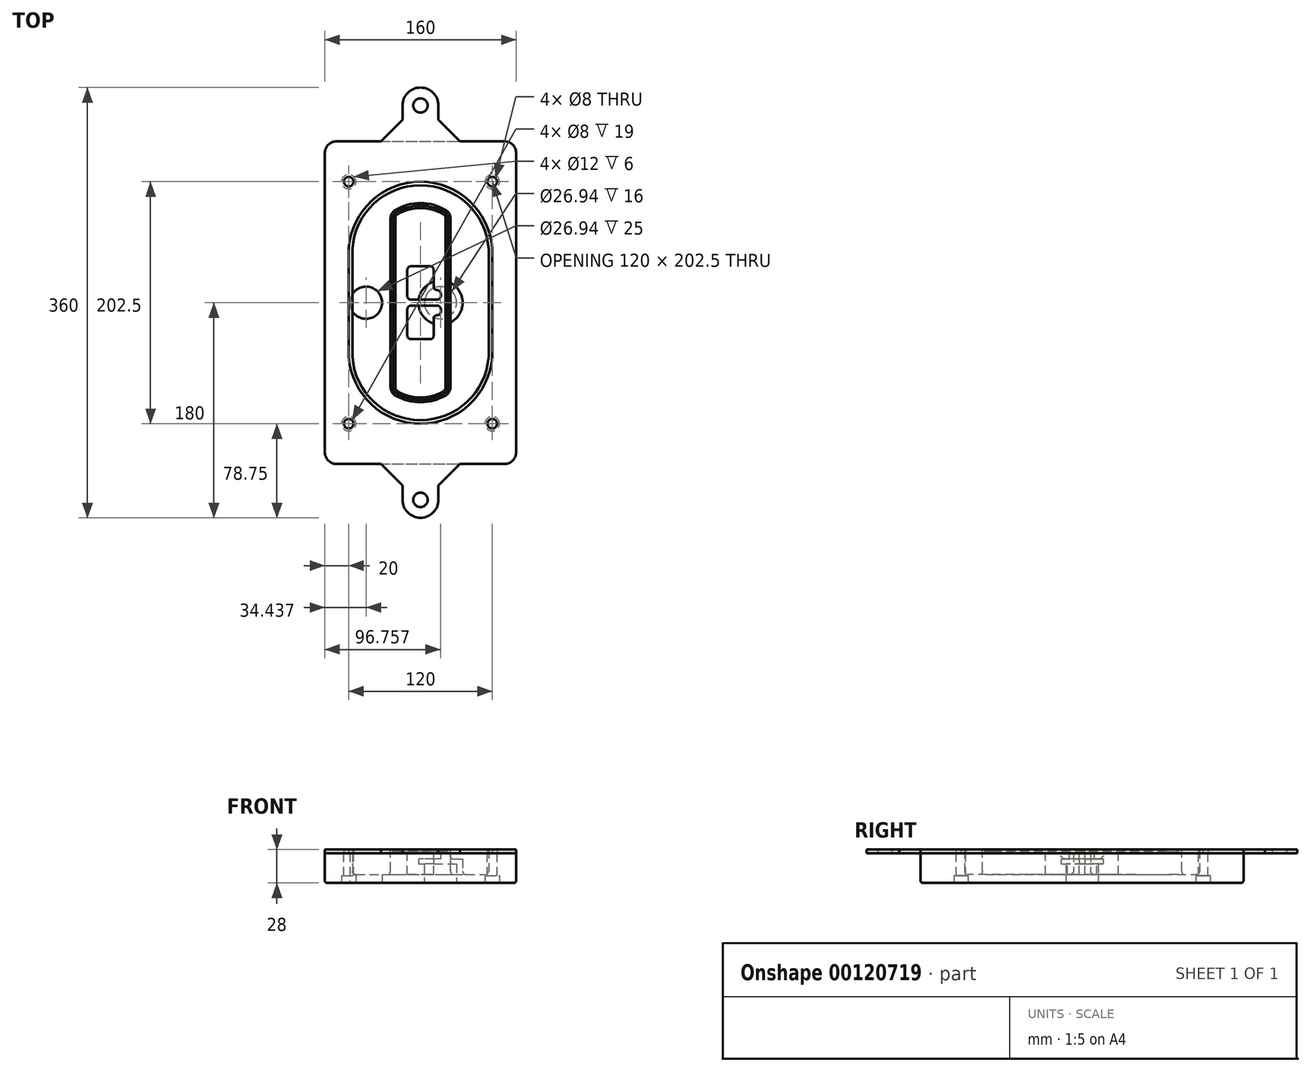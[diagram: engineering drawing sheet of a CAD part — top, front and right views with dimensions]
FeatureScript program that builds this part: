
annotation { "Feature Type Name" : "Feature", "Feature Type Description" : "" }
export const myFeature = defineFeature(function(context is Context, id is Id, definition is map)
    precondition{}
    {
        {
            var Q0;
            Q0=qCreatedBy(makeId("Top.planeOp"),FACE);
            var sketch = newSketch(context, id + "F0", { "sketchPlane" : qUnion([Q0])});
            skPoint(sketch, "E0.rect.middle", {"position": v(0, 0) * mm});
            skLineSegment(sketch, "E1.bottom", {"start": v(-70, -135) * mm, "end": v(70, -135) * mm});
            skLineSegment(sketch, "E1.top", {"start": v(-70, 135) * mm, "end": v(70, 135) * mm});
            skLineSegment(sketch, "E1.left", {"start": v(-80, -125) * mm, "end": v(-80, 125) * mm});
            skLineSegment(sketch, "E1.right", {"start": v(80, -125) * mm, "end": v(80, 125) * mm});
            skLineSegment(sketch, "E2", {"start": v(-80, 135) * mm, "end": v(80, -135) * mm, "construction": true});
            skLineSegment(sketch, "E3", {"start": v(80, 135) * mm, "end": v(-80, -135) * mm, "construction": true});
            skCircle(sketch, "E4", {"center": v(-60, 101.25) * mm, "radius": 4 * mm});
            skCircle(sketch, "E5", {"center": v(60, 101.25) * mm, "radius": 4 * mm});
            skCircle(sketch, "E6", {"center": v(60, -101.25) * mm, "radius": 4 * mm});
            skCircle(sketch, "E7", {"center": v(-60, -101.25) * mm, "radius": 4 * mm});
            skLineSegment(sketch, "E8", {"start": v(-60, 101.25) * mm, "end": v(60, 101.25) * mm, "construction": true});
            skLineSegment(sketch, "E9", {"start": v(60, 101.25) * mm, "end": v(60, -101.25) * mm, "construction": true});
            skLineSegment(sketch, "E10", {"start": v(60, -101.25) * mm, "end": v(-60, -101.25) * mm, "construction": true});
            skLineSegment(sketch, "E11", {"start": v(-60, -101.25) * mm, "end": v(-60, 101.25) * mm, "construction": true});
            skLineSegment(sketch, "E12", {"start": v(-60, 44.66) * mm, "end": v(-60, -44.66) * mm});
            skLineSegment(sketch, "E13", {"start": v(60, 44.66) * mm, "end": v(60, -44.66) * mm});
            skArc(sketch, "E14", {"start": v(59.98, 45.37) * mm, "mid": v(0, 101.25) * mm, "end": v(-59.98, 45.37) * mm});
            skArc(sketch, "E15", {"start": v(-59.98, -45.37) * mm, "mid": v(0, -101.25) * mm, "end": v(59.98, -45.37) * mm});
            skLineSegment(sketch, "E16", {"start": v(-60, 0) * mm, "end": v(60, 0) * mm, "construction": true});
            skPoint(sketch, "E17.visualSharp", {"position": v(-60, -45) * mm});
            skArc(sketch, "E17.filletArc", {"start": v(-60, -44.66) * mm, "mid": v(-60, -45.02) * mm, "end": v(-59.98, -45.37) * mm});
            skPoint(sketch, "E18.visualSharp", {"position": v(-60, 45) * mm});
            skArc(sketch, "E18.filletArc", {"start": v(-59.98, 45.37) * mm, "mid": v(-60, 45.02) * mm, "end": v(-60, 44.66) * mm});
            skPoint(sketch, "E19.visualSharp", {"position": v(60, 45) * mm});
            skArc(sketch, "E19.filletArc", {"start": v(60, 44.66) * mm, "mid": v(60, 45.02) * mm, "end": v(59.98, 45.37) * mm});
            skPoint(sketch, "E20.visualSharp", {"position": v(60, -45) * mm});
            skArc(sketch, "E20.filletArc", {"start": v(59.98, -45.37) * mm, "mid": v(60, -45.02) * mm, "end": v(60, -44.66) * mm});
            skPoint(sketch, "E21.visualSharp", {"position": v(-80, 135) * mm});
            skArc(sketch, "E21.filletArc", {"start": v(-70, 135) * mm, "mid": v(-77.07, 132.07) * mm, "end": v(-80, 125) * mm});
            skPoint(sketch, "E22.visualSharp", {"position": v(80, 135) * mm});
            skArc(sketch, "E22.filletArc", {"start": v(80, 125) * mm, "mid": v(77.07, 132.07) * mm, "end": v(70, 135) * mm});
            skPoint(sketch, "E23.visualSharp", {"position": v(80, -135) * mm});
            skArc(sketch, "E23.filletArc", {"start": v(70, -135) * mm, "mid": v(77.07, -132.07) * mm, "end": v(80, -125) * mm});
            skPoint(sketch, "E24.visualSharp", {"position": v(-80, -135) * mm});
            skArc(sketch, "E24.filletArc", {"start": v(-80, -125) * mm, "mid": v(-77.07, -132.07) * mm, "end": v(-70, -135) * mm});
            skArc(sketch, "E25.0", {"start": v(57, 44.66) * mm, "mid": v(57, 44.9) * mm, "end": v(56.98, 45.16) * mm});
            skLineSegment(sketch, "E25.1", {"start": v(57, 44.66) * mm, "end": v(57, -44.66) * mm});
            skArc(sketch, "E25.2", {"start": v(56.98, -45.16) * mm, "mid": v(57, -44.9) * mm, "end": v(57, -44.66) * mm});
            skArc(sketch, "E25.3", {"start": v(-56.98, -45.16) * mm, "mid": v(0, -98.25) * mm, "end": v(56.98, -45.16) * mm});
            skArc(sketch, "E25.4", {"start": v(-57, -44.66) * mm, "mid": v(-57, -44.9) * mm, "end": v(-56.98, -45.16) * mm});
            skArc(sketch, "E25.5", {"start": v(56.98, 45.16) * mm, "mid": v(0, 98.25) * mm, "end": v(-56.98, 45.16) * mm});
            skLineSegment(sketch, "E25.6", {"start": v(-57, 44.66) * mm, "end": v(-57, -44.66) * mm});
            skArc(sketch, "E25.7", {"start": v(-56.98, 45.16) * mm, "mid": v(-57, 44.9) * mm, "end": v(-57, 44.66) * mm});
            skArc(sketch, "E26.0", {"start": v(-63.97, 45.65) * mm, "mid": v(-64, 45.16) * mm, "end": v(-64, 44.66) * mm});
            skArc(sketch, "E26.1", {"start": v(63.97, 45.65) * mm, "mid": v(0, 105.25) * mm, "end": v(-63.97, 45.65) * mm});
            skArc(sketch, "E26.2", {"start": v(64, 44.66) * mm, "mid": v(64, 45.16) * mm, "end": v(63.97, 45.65) * mm});
            skLineSegment(sketch, "E26.3", {"start": v(64, 44.66) * mm, "end": v(64, -44.66) * mm});
            skArc(sketch, "E26.4", {"start": v(63.97, -45.65) * mm, "mid": v(64, -45.16) * mm, "end": v(64, -44.66) * mm});
            skLineSegment(sketch, "E26.5", {"start": v(-64, 44.66) * mm, "end": v(-64, -44.66) * mm});
            skArc(sketch, "E26.6", {"start": v(-63.97, -45.65) * mm, "mid": v(0, -105.25) * mm, "end": v(63.97, -45.65) * mm});
            skArc(sketch, "E26.7", {"start": v(-64, -44.66) * mm, "mid": v(-64, -45.16) * mm, "end": v(-63.97, -45.65) * mm});
            skSolve(sketch);
        }
        {
            var Q0;
            Q0=makeQuery(id+"F0.imprint","IMPRINT",FACE,{"disambiguationData":[TD([[makeQuery(id+"F0.imprint","IMPRINT",EDGE,{"derivedFrom":sQuery(id+"F0.wireOp",EDGE,"E1.bottom")}),1.0]])]});
            var Q1;
            Q1=makeQuery(id+"F0.imprint","IMPRINT",FACE,{"disambiguationData":[TD([[makeQuery(id+"F0.imprint","IMPRINT",EDGE,{"derivedFrom":sQuery(id+"F0.wireOp",EDGE,"E12")}),1.0]])]});
            var Q2;
            Q2=makeQuery(id+"F0.imprint","IMPRINT",FACE,{"disambiguationData":[TD([[makeQuery(id+"F0.imprint","IMPRINT",EDGE,{"derivedFrom":sQuery(id+"F0.wireOp",EDGE,"E25.0")}),1.0]])]});
            var Q3;
            Q3=makeQuery(id+"F0.imprint","IMPRINT",FACE,{"disambiguationData":[TD([[makeQuery(id+"F0.imprint","IMPRINT",EDGE,{"derivedFrom":sQuery(id+"F0.wireOp",EDGE,"E12")}),-1.0]])]});
            extrude(context, id + "F1", {"entities" : qUnion([Q0, Q1, Q2, Q3]), "oppositeDirection" : true, "depth" : 25 * mm});
        }
        {
            var Q0;
            Q0=makeQuery(id+"F0.imprint","IMPRINT",FACE,{"disambiguationData":[TD([[makeQuery(id+"F0.imprint","IMPRINT",EDGE,{"derivedFrom":sQuery(id+"F0.wireOp",EDGE,"E12")}),1.0]])]});
            extrude(context, id + "F2", {"entities" : qUnion([Q0]), "operationType" : NewBodyOperationType.ADD, "depth" : 3 * mm});
        }
        {
            var Q0;
            Q0=makeQuery(id+"F0.imprint","IMPRINT",FACE,{"disambiguationData":[TD([[makeQuery(id+"F0.imprint","IMPRINT",EDGE,{"derivedFrom":sQuery(id+"F0.wireOp",EDGE,"E25.0")}),1.0]])]});
            extrude(context, id + "F3", {"entities" : qUnion([Q0]), "operationType" : NewBodyOperationType.REMOVE, "oppositeDirection" : true, "depth" : 18 * mm});
        }
        {
            var Q0;
            Q0=makeQuery(id+"F2.opExtrude","CAP_FACE",FACE,{"disambiguationData":[OSD([sQuery(id+"F0.wireOp",EDGE,"E12"),sQuery(id+"F0.wireOp",EDGE,"E13"),sQuery(id+"F0.wireOp",EDGE,"E14"),sQuery(id+"F0.wireOp",EDGE,"E15"),sQuery(id+"F0.wireOp",EDGE,"E17.filletArc"),sQuery(id+"F0.wireOp",EDGE,"E18.filletArc"),sQuery(id+"F0.wireOp",EDGE,"E19.filletArc"),sQuery(id+"F0.wireOp",EDGE,"E20.filletArc"),sQuery(id+"F0.wireOp",EDGE,"E25.0"),sQuery(id+"F0.wireOp",EDGE,"E25.1"),sQuery(id+"F0.wireOp",EDGE,"E25.2"),sQuery(id+"F0.wireOp",EDGE,"E25.3"),sQuery(id+"F0.wireOp",EDGE,"E25.4"),sQuery(id+"F0.wireOp",EDGE,"E25.5"),sQuery(id+"F0.wireOp",EDGE,"E25.6"),sQuery(id+"F0.wireOp",EDGE,"E25.7")])],"isStart":false});
            var sketch = newSketch(context, id + "F4", { "sketchPlane" : qUnion([Q0])});
            skArc(sketch, "E27.0", {"start": v(-20.99, -77.65) * mm, "mid": v(0, -83.25) * mm, "end": v(20.99, -77.65) * mm});
            skArc(sketch, "E28.0", {"start": v(20.99, 77.65) * mm, "mid": v(0, 83.25) * mm, "end": v(-20.99, 77.65) * mm});
            skLineSegment(sketch, "E29", {"start": v(-25, 70.71) * mm, "end": v(-25, -70.71) * mm});
            skLineSegment(sketch, "E30", {"start": v(25, 70.71) * mm, "end": v(25, -70.71) * mm});
            skLineSegment(sketch, "E31", {"start": v(-25, 75.03) * mm, "end": v(25, 75.03) * mm, "construction": true});
            skLineSegment(sketch, "E32", {"start": v(-25, -75.03) * mm, "end": v(25, -75.03) * mm, "construction": true});
            skPoint(sketch, "E33.visualSharp", {"position": v(-25, 75.03) * mm});
            skArc(sketch, "E33.filletArc", {"start": v(-20.99, 77.65) * mm, "mid": v(-23.92, 74.72) * mm, "end": v(-25, 70.71) * mm});
            skPoint(sketch, "E34.visualSharp", {"position": v(25, 75.03) * mm});
            skArc(sketch, "E34.filletArc", {"start": v(25, 70.71) * mm, "mid": v(23.92, 74.72) * mm, "end": v(20.99, 77.65) * mm});
            skPoint(sketch, "E35.visualSharp", {"position": v(25, -75.03) * mm});
            skArc(sketch, "E35.filletArc", {"start": v(20.99, -77.65) * mm, "mid": v(23.92, -74.72) * mm, "end": v(25, -70.71) * mm});
            skPoint(sketch, "E36.visualSharp", {"position": v(-25, -75.03) * mm});
            skArc(sketch, "E36.filletArc", {"start": v(-25, -70.71) * mm, "mid": v(-23.92, -74.72) * mm, "end": v(-20.99, -77.65) * mm});
            skArc(sketch, "E37.0", {"start": v(56.98, 45.16) * mm, "mid": v(0, 98.25) * mm, "end": v(-56.98, 45.16) * mm});
            skArc(sketch, "E37.1", {"start": v(-56.98, 45.16) * mm, "mid": v(-57, 44.9) * mm, "end": v(-57, 44.66) * mm});
            skLineSegment(sketch, "E37.2", {"start": v(-57, 44.66) * mm, "end": v(-57, -44.66) * mm});
            skArc(sketch, "E37.3", {"start": v(-57, -44.66) * mm, "mid": v(-57, -44.9) * mm, "end": v(-56.98, -45.16) * mm});
            skArc(sketch, "E37.4", {"start": v(-56.98, -45.16) * mm, "mid": v(0, -98.25) * mm, "end": v(56.98, -45.16) * mm});
            skArc(sketch, "E37.5", {"start": v(56.98, -45.16) * mm, "mid": v(57, -44.9) * mm, "end": v(57, -44.66) * mm});
            skLineSegment(sketch, "E37.6", {"start": v(57, 44.66) * mm, "end": v(57, -44.66) * mm});
            skArc(sketch, "E37.7", {"start": v(57, 44.66) * mm, "mid": v(57, 44.9) * mm, "end": v(56.98, 45.16) * mm});
            skLineSegment(sketch, "E38.0", {"start": v(23, 70.71) * mm, "end": v(23, -70.71) * mm});
            skArc(sketch, "E38.1", {"start": v(19.99, -75.92) * mm, "mid": v(22.2, -73.72) * mm, "end": v(23, -70.71) * mm});
            skArc(sketch, "E38.2", {"start": v(-19.99, -75.92) * mm, "mid": v(0, -81.25) * mm, "end": v(19.99, -75.92) * mm});
            skArc(sketch, "E38.3", {"start": v(-23, -70.71) * mm, "mid": v(-22.2, -73.72) * mm, "end": v(-19.99, -75.92) * mm});
            skLineSegment(sketch, "E38.4", {"start": v(-23, 70.71) * mm, "end": v(-23, -70.71) * mm});
            skArc(sketch, "E38.5", {"start": v(23, 70.71) * mm, "mid": v(22.2, 73.72) * mm, "end": v(19.99, 75.92) * mm});
            skArc(sketch, "E38.6", {"start": v(-19.99, 75.92) * mm, "mid": v(-22.2, 73.72) * mm, "end": v(-23, 70.71) * mm});
            skArc(sketch, "E38.7", {"start": v(19.99, 75.92) * mm, "mid": v(0, 81.25) * mm, "end": v(-19.99, 75.92) * mm});
            skArc(sketch, "E39.0", {"start": v(21, 70.71) * mm, "mid": v(20.46, 72.72) * mm, "end": v(19, 74.18) * mm});
            skLineSegment(sketch, "E39.1", {"start": v(21, 70.71) * mm, "end": v(21, -70.71) * mm});
            skArc(sketch, "E39.2", {"start": v(19, -74.18) * mm, "mid": v(20.46, -72.72) * mm, "end": v(21, -70.71) * mm});
            skArc(sketch, "E39.3", {"start": v(-19, -74.18) * mm, "mid": v(0, -79.25) * mm, "end": v(19, -74.18) * mm});
            skArc(sketch, "E39.4", {"start": v(-21, -70.71) * mm, "mid": v(-20.46, -72.72) * mm, "end": v(-19, -74.18) * mm});
            skArc(sketch, "E39.5", {"start": v(19, 74.18) * mm, "mid": v(0, 79.25) * mm, "end": v(-19, 74.18) * mm});
            skLineSegment(sketch, "E39.6", {"start": v(-21, 70.71) * mm, "end": v(-21, -70.71) * mm});
            skArc(sketch, "E39.7", {"start": v(-19, 74.18) * mm, "mid": v(-20.46, 72.72) * mm, "end": v(-21, 70.71) * mm});
            skLineSegment(sketch, "E40", {"start": v(-25, 0) * mm, "end": v(25, 0) * mm, "construction": true});
            skLineSegment(sketch, "E41", {"start": v(-11, 5.5) * mm, "end": v(-11, 27.5) * mm});
            skLineSegment(sketch, "E42", {"start": v(-8, 30.5) * mm, "end": v(8, 30.5) * mm});
            skLineSegment(sketch, "E43", {"start": v(11, 27.5) * mm, "end": v(11, 13.5) * mm});
            skLineSegment(sketch, "E44", {"start": v(14, 10.5) * mm, "end": v(14, 10.5) * mm});
            skLineSegment(sketch, "E45", {"start": v(17, 7.5) * mm, "end": v(17, 5.5) * mm});
            skLineSegment(sketch, "E46", {"start": v(14, 2.5) * mm, "end": v(-8, 2.5) * mm});
            skPoint(sketch, "E47.visualSharp", {"position": v(-11, 30.5) * mm});
            skArc(sketch, "E47.filletArc", {"start": v(-8, 30.5) * mm, "mid": v(-10.12, 29.62) * mm, "end": v(-11, 27.5) * mm});
            skPoint(sketch, "E48.visualSharp", {"position": v(11, 30.5) * mm});
            skArc(sketch, "E48.filletArc", {"start": v(11, 27.5) * mm, "mid": v(10.12, 29.62) * mm, "end": v(8, 30.5) * mm});
            skPoint(sketch, "E49.visualSharp", {"position": v(11, 10.5) * mm});
            skArc(sketch, "E49.filletArc", {"start": v(11, 13.5) * mm, "mid": v(11.88, 11.38) * mm, "end": v(14, 10.5) * mm});
            skPoint(sketch, "E50.visualSharp", {"position": v(17, 10.5) * mm});
            skArc(sketch, "E50.filletArc", {"start": v(17, 7.5) * mm, "mid": v(16.12, 9.62) * mm, "end": v(14, 10.5) * mm});
            skPoint(sketch, "E51.visualSharp", {"position": v(17, 2.5) * mm});
            skArc(sketch, "E51.filletArc", {"start": v(14, 2.5) * mm, "mid": v(16.12, 3.38) * mm, "end": v(17, 5.5) * mm});
            skPoint(sketch, "E52.visualSharp", {"position": v(-11, 2.5) * mm});
            skArc(sketch, "E52.filletArc", {"start": v(-11, 5.5) * mm, "mid": v(-10.12, 3.38) * mm, "end": v(-8, 2.5) * mm});
            skLineSegment(sketch, "E53.0.MirrorCS", {"start": v(14, -2.5) * mm, "end": v(-8, -2.5) * mm});
            skArc(sketch, "E54.0.MirrorCS", {"start": v(-11, -5.5) * mm, "mid": v(-10.12, -3.38) * mm, "end": v(-8, -2.5) * mm});
            skLineSegment(sketch, "E55.0.MirrorCS", {"start": v(-11, -5.5) * mm, "end": v(-11, -27.5) * mm});
            skArc(sketch, "E56.0.MirrorCS", {"start": v(-8, -30.5) * mm, "mid": v(-10.12, -29.62) * mm, "end": v(-11, -27.5) * mm});
            skLineSegment(sketch, "E57.0.MirrorCS", {"start": v(-8, -30.5) * mm, "end": v(8, -30.5) * mm});
            skArc(sketch, "E58.0.MirrorCS", {"start": v(11, -27.5) * mm, "mid": v(10.12, -29.62) * mm, "end": v(8, -30.5) * mm});
            skLineSegment(sketch, "E59.0.MirrorCS", {"start": v(11, -27.5) * mm, "end": v(11, -13.5) * mm});
            skArc(sketch, "E60.0.MirrorCS", {"start": v(11, -13.5) * mm, "mid": v(11.88, -11.38) * mm, "end": v(14, -10.5) * mm});
            skArc(sketch, "E61.0.MirrorCS", {"start": v(17, -7.5) * mm, "mid": v(16.12, -9.62) * mm, "end": v(14, -10.5) * mm});
            skLineSegment(sketch, "E62.0.MirrorCS", {"start": v(17, -7.5) * mm, "end": v(17, -5.5) * mm});
            skArc(sketch, "E63.0.MirrorCS", {"start": v(14, -2.5) * mm, "mid": v(16.12, -3.38) * mm, "end": v(17, -5.5) * mm});
            skSolve(sketch);
        }
        {
            var Q0;
            Q0=makeQuery(id+"F4.imprint","IMPRINT",FACE,{"disambiguationData":[TD([[makeQuery(id+"F4.imprint","IMPRINT",EDGE,{"derivedFrom":sQuery(id+"F4.wireOp",EDGE,"E27.0")}),1.0]])]});
            var Q1;
            Q1=makeQuery(id+"F4.imprint","IMPRINT",FACE,{"disambiguationData":[TD([[makeQuery(id+"F4.imprint","IMPRINT",EDGE,{"derivedFrom":sQuery(id+"F4.wireOp",EDGE,"E38.0")}),-1.0]])]});
            var Q2;
            Q2=makeQuery(id+"F4.imprint","IMPRINT",FACE,{"disambiguationData":[TD([[makeQuery(id+"F4.imprint","IMPRINT",EDGE,{"derivedFrom":sQuery(id+"F4.wireOp",EDGE,"E39.0")}),1.0]])]});
            extrude(context, id + "F5", {"entities" : qUnion([Q0, Q1, Q2]), "operationType" : NewBodyOperationType.ADD, "endBound" : BoundingType.UP_TO_NEXT, "oppositeDirection" : true, "depth" : 25 * mm});
        }
        {
            var Q0;
            Q0=makeQuery(id+"F4.imprint","IMPRINT",FACE,{"disambiguationData":[TD([[makeQuery(id+"F4.imprint","IMPRINT",EDGE,{"derivedFrom":sQuery(id+"F4.wireOp",EDGE,"E38.0")}),-1.0]])]});
            extrude(context, id + "F6", {"entities" : qUnion([Q0]), "operationType" : NewBodyOperationType.REMOVE, "oppositeDirection" : true, "depth" : 2 * mm});
        }
        {
            var Q0;
            Q0=makeQuery(id+"F1.opExtrude","CAP_FACE",FACE,{"disambiguationData":[OSD([sQuery(id+"F0.wireOp",EDGE,"E1.bottom"),sQuery(id+"F0.wireOp",EDGE,"E1.top"),sQuery(id+"F0.wireOp",EDGE,"E1.left"),sQuery(id+"F0.wireOp",EDGE,"E1.right"),sQuery(id+"F0.wireOp",EDGE,"E4"),sQuery(id+"F0.wireOp",EDGE,"E5"),sQuery(id+"F0.wireOp",EDGE,"E6"),sQuery(id+"F0.wireOp",EDGE,"E7"),sQuery(id+"F0.wireOp",EDGE,"E21.filletArc"),sQuery(id+"F0.wireOp",EDGE,"E22.filletArc"),sQuery(id+"F0.wireOp",EDGE,"E23.filletArc"),sQuery(id+"F0.wireOp",EDGE,"E24.filletArc")])],"isStart":false});
            var sketch = newSketch(context, id + "F7", { "sketchPlane" : qUnion([Q0])});
            skCircle(sketch, "E64", {"center": v(16.76, 0) * mm, "radius": 13.47 * mm});
            skCircle(sketch, "E65", {"center": v(-45.56, 0) * mm, "radius": 13.47 * mm});
            skLineSegment(sketch, "E66", {"start": v(80, 0) * mm, "end": v(-80, 0) * mm});
            skCircle(sketch, "E67", {"center": v(16.76, 0) * mm, "radius": 18.47 * mm});
            skCircle(sketch, "E68", {"center": v(60, -101.25) * mm, "radius": 6 * mm});
            skCircle(sketch, "E69", {"center": v(-60, -101.25) * mm, "radius": 6 * mm});
            skCircle(sketch, "E70", {"center": v(-60, 101.25) * mm, "radius": 6 * mm});
            skCircle(sketch, "E71", {"center": v(60, 101.25) * mm, "radius": 6 * mm});
            skSolve(sketch);
        }
        {
            var Q0;
            {var subQ1=sQuery(id+"F7.wireOp",EDGE,"E66");var subQ4=sQuery(id+"F7.wireOp",EDGE,"E64");var subQ6=makeQuery(id+"F7.imprint","INTERSECT",VERTEX,{"disambiguationData":[OD(0.0)],"derivedFrom":[subQ4,subQ1]});Q0=makeQuery(id+"F7.imprint","IMPRINT",FACE,{"disambiguationData":[TD([[makeQuery(id+"F7.imprint","IMPRINT",EDGE,{"disambiguationData":[TD([[subQ6,-1.0]])],"derivedFrom":subQ4}),-1.0]])]});}
            var Q1;
            {var subQ0=sQuery(id+"F7.wireOp",EDGE,"E66");var subQ1=sQuery(id+"F7.wireOp",EDGE,"E64");var subQ3=makeQuery(id+"F7.imprint","INTERSECT",VERTEX,{"disambiguationData":[OD(0.0)],"derivedFrom":[subQ1,subQ0]});Q1=makeQuery(id+"F7.imprint","IMPRINT",FACE,{"disambiguationData":[TD([[makeQuery(id+"F7.imprint","IMPRINT",EDGE,{"disambiguationData":[TD([[subQ3,-1.0]])],"derivedFrom":subQ1}),1.0]])]});}
            var Q2;
            {var subQ0=sQuery(id+"F7.wireOp",EDGE,"E66");var subQ1=sQuery(id+"F7.wireOp",EDGE,"E64");var subQ3=makeQuery(id+"F7.imprint","INTERSECT",VERTEX,{"disambiguationData":[OD(0.0)],"derivedFrom":[subQ1,subQ0]});Q2=makeQuery(id+"F7.imprint","IMPRINT",FACE,{"disambiguationData":[TD([[makeQuery(id+"F7.imprint","IMPRINT",EDGE,{"disambiguationData":[TD([[subQ3,1.0]])],"derivedFrom":subQ1}),1.0]])]});}
            var Q3;
            {var subQ1=sQuery(id+"F7.wireOp",EDGE,"E66");var subQ4=sQuery(id+"F7.wireOp",EDGE,"E64");var subQ6=makeQuery(id+"F7.imprint","INTERSECT",VERTEX,{"disambiguationData":[OD(0.0)],"derivedFrom":[subQ4,subQ1]});Q3=makeQuery(id+"F7.imprint","IMPRINT",FACE,{"disambiguationData":[TD([[makeQuery(id+"F7.imprint","IMPRINT",EDGE,{"disambiguationData":[TD([[subQ6,1.0]])],"derivedFrom":subQ4}),-1.0]])]});}
            extrude(context, id + "F8", {"entities" : qUnion([Q0, Q1, Q2, Q3]), "operationType" : NewBodyOperationType.ADD, "oppositeDirection" : true, "depth" : 20 * mm});
        }
        {
            var Q0;
            {var subQ0=sQuery(id+"F7.wireOp",EDGE,"E66");var subQ1=sQuery(id+"F7.wireOp",EDGE,"E64");var subQ3=makeQuery(id+"F7.imprint","INTERSECT",VERTEX,{"disambiguationData":[OD(0.0)],"derivedFrom":[subQ1,subQ0]});Q0=makeQuery(id+"F7.imprint","IMPRINT",FACE,{"disambiguationData":[TD([[makeQuery(id+"F7.imprint","IMPRINT",EDGE,{"disambiguationData":[TD([[subQ3,-1.0]])],"derivedFrom":subQ1}),1.0]])]});}
            var Q1;
            {var subQ0=sQuery(id+"F7.wireOp",EDGE,"E66");var subQ1=sQuery(id+"F7.wireOp",EDGE,"E64");var subQ3=makeQuery(id+"F7.imprint","INTERSECT",VERTEX,{"disambiguationData":[OD(0.0)],"derivedFrom":[subQ1,subQ0]});Q1=makeQuery(id+"F7.imprint","IMPRINT",FACE,{"disambiguationData":[TD([[makeQuery(id+"F7.imprint","IMPRINT",EDGE,{"disambiguationData":[TD([[subQ3,1.0]])],"derivedFrom":subQ1}),1.0]])]});}
            extrude(context, id + "F9", {"entities" : qUnion([Q0, Q1]), "operationType" : NewBodyOperationType.REMOVE, "oppositeDirection" : true, "depth" : 16 * mm});
        }
        {
            var Q0;
            {var subQ0=sQuery(id+"F7.wireOp",EDGE,"E66");var subQ1=sQuery(id+"F7.wireOp",EDGE,"E65");var subQ3=makeQuery(id+"F7.imprint","INTERSECT",VERTEX,{"disambiguationData":[OD(0.0)],"derivedFrom":[subQ1,subQ0]});Q0=makeQuery(id+"F7.imprint","IMPRINT",FACE,{"disambiguationData":[TD([[makeQuery(id+"F7.imprint","IMPRINT",EDGE,{"disambiguationData":[TD([[subQ3,-1.0]])],"derivedFrom":subQ1}),1.0]])]});}
            var Q1;
            {var subQ0=sQuery(id+"F7.wireOp",EDGE,"E66");var subQ1=sQuery(id+"F7.wireOp",EDGE,"E65");var subQ3=makeQuery(id+"F7.imprint","INTERSECT",VERTEX,{"disambiguationData":[OD(0.0)],"derivedFrom":[subQ1,subQ0]});Q1=makeQuery(id+"F7.imprint","IMPRINT",FACE,{"disambiguationData":[TD([[makeQuery(id+"F7.imprint","IMPRINT",EDGE,{"disambiguationData":[TD([[subQ3,1.0]])],"derivedFrom":subQ1}),1.0]])]});}
            extrude(context, id + "F10", {"entities" : qUnion([Q0, Q1]), "operationType" : NewBodyOperationType.REMOVE, "oppositeDirection" : true, "depth" : 25 * mm});
        }
        {
            var Q0;
            Q0=makeQuery(id+"F7.imprint","IMPRINT",FACE,{"disambiguationData":[TD([[makeQuery(id+"F7.imprint","IMPRINT",EDGE,{"derivedFrom":sQuery(id+"F7.wireOp",EDGE,"E68")}),1.0]])]});
            var Q1;
            Q1=makeQuery(id+"F7.imprint","IMPRINT",FACE,{"disambiguationData":[TD([[makeQuery(id+"F7.imprint","IMPRINT",EDGE,{"derivedFrom":makeQuery(id+"F1.opExtrude","CAP_EDGE",EDGE,{"disambiguationData":[OSD([sQuery(id+"F0.wireOp",EDGE,"E5")])],"isStart":false})}),-1.0]])]});
            var Q2;
            Q2=makeQuery(id+"F7.imprint","IMPRINT",FACE,{"disambiguationData":[TD([[makeQuery(id+"F7.imprint","IMPRINT",EDGE,{"derivedFrom":sQuery(id+"F7.wireOp",EDGE,"E69")}),1.0]])]});
            var Q3;
            Q3=makeQuery(id+"F7.imprint","IMPRINT",FACE,{"disambiguationData":[TD([[makeQuery(id+"F7.imprint","IMPRINT",EDGE,{"derivedFrom":makeQuery(id+"F1.opExtrude","CAP_EDGE",EDGE,{"disambiguationData":[OSD([sQuery(id+"F0.wireOp",EDGE,"E4")])],"isStart":false})}),-1.0]])]});
            var Q4;
            Q4=makeQuery(id+"F7.imprint","IMPRINT",FACE,{"disambiguationData":[TD([[makeQuery(id+"F7.imprint","IMPRINT",EDGE,{"derivedFrom":sQuery(id+"F7.wireOp",EDGE,"E70")}),1.0]])]});
            var Q5;
            Q5=makeQuery(id+"F7.imprint","IMPRINT",FACE,{"disambiguationData":[TD([[makeQuery(id+"F7.imprint","IMPRINT",EDGE,{"derivedFrom":makeQuery(id+"F1.opExtrude","CAP_EDGE",EDGE,{"disambiguationData":[OSD([sQuery(id+"F0.wireOp",EDGE,"E7")])],"isStart":false})}),-1.0]])]});
            var Q6;
            Q6=makeQuery(id+"F7.imprint","IMPRINT",FACE,{"disambiguationData":[TD([[makeQuery(id+"F7.imprint","IMPRINT",EDGE,{"derivedFrom":sQuery(id+"F7.wireOp",EDGE,"E71")}),1.0]])]});
            var Q7;
            Q7=makeQuery(id+"F7.imprint","IMPRINT",FACE,{"disambiguationData":[TD([[makeQuery(id+"F7.imprint","IMPRINT",EDGE,{"derivedFrom":makeQuery(id+"F1.opExtrude","CAP_EDGE",EDGE,{"disambiguationData":[OSD([sQuery(id+"F0.wireOp",EDGE,"E6")])],"isStart":false})}),-1.0]])]});
            extrude(context, id + "F11", {"entities" : qUnion([Q0, Q1, Q2, Q3, Q4, Q5, Q6, Q7]), "operationType" : NewBodyOperationType.REMOVE, "oppositeDirection" : true, "depth" : 6 * mm});
        }
        {
            var Q0;
            Q0=makeQuery(id+"F9.boolean.opBoolean","COPY",FACE,{"derivedFrom":makeQuery(id+"F9.opExtrude","CAP_FACE",FACE,{"disambiguationData":[OSD([sQuery(id+"F7.wireOp",EDGE,"E64")])],"isStart":false})});
            var sketch = newSketch(context, id + "F12", { "sketchPlane" : qUnion([Q0])});
            skArc(sketch, "E72.0", {"start": v(11, 17.55) * mm, "mid": v(2.57, 11.82) * mm, "end": v(-1.54, 2.5) * mm});
            skArc(sketch, "E72.1", {"start": v(-1.54, -2.5) * mm, "mid": v(2.57, -11.82) * mm, "end": v(11, -17.55) * mm});
            skLineSegment(sketch, "E73", {"start": v(-1.54, -2.5) * mm, "end": v(14, -2.5) * mm});
            skLineSegment(sketch, "E74.0", {"start": v(14, 2.5) * mm, "end": v(-1.54, 2.5) * mm});
            skArc(sketch, "E74.1", {"start": v(14, 2.5) * mm, "mid": v(16.12, 3.38) * mm, "end": v(17, 5.5) * mm});
            skLineSegment(sketch, "E74.2", {"start": v(17, 7.5) * mm, "end": v(17, 5.5) * mm});
            skArc(sketch, "E74.3", {"start": v(17, 7.5) * mm, "mid": v(16.12, 9.62) * mm, "end": v(14, 10.5) * mm});
            skArc(sketch, "E74.4", {"start": v(11, 13.5) * mm, "mid": v(11.88, 11.38) * mm, "end": v(14, 10.5) * mm});
            skLineSegment(sketch, "E74.5", {"start": v(11, 17.55) * mm, "end": v(11, 13.5) * mm});
            skLineSegment(sketch, "E74.7", {"start": v(14, -2.5) * mm, "end": v(-1.54, -2.5) * mm});
            skArc(sketch, "E74.8", {"start": v(14, -2.5) * mm, "mid": v(16.12, -3.38) * mm, "end": v(17, -5.5) * mm});
            skLineSegment(sketch, "E74.9", {"start": v(17, -7.5) * mm, "end": v(17, -5.5) * mm});
            skArc(sketch, "E74.10", {"start": v(17, -7.5) * mm, "mid": v(16.12, -9.62) * mm, "end": v(14, -10.5) * mm});
            skArc(sketch, "E74.11", {"start": v(11, -13.5) * mm, "mid": v(11.88, -11.38) * mm, "end": v(14, -10.5) * mm});
            skLineSegment(sketch, "E74.12", {"start": v(11, -17.55) * mm, "end": v(11, -13.5) * mm});
            skPoint(sketch, "E75.orphan", {"position": v(11, -27.5) * mm});
            skPoint(sketch, "E76.orphan", {"position": v(-8, -2.5) * mm});
            skPoint(sketch, "E77.orphan", {"position": v(-8, 2.5) * mm});
            skPoint(sketch, "E78.orphan", {"position": v(11, 27.5) * mm});
            skSolve(sketch);
        }
        {
            var Q0;
            {var subQ7=sQuery(id+"F12.wireOp",EDGE,"E72.0");var subQ14=sQuery(id+"F12.wireOp",EDGE,"E72.1");var subQ16=sQuery(id+"F12.wireOp",EDGE,"E74.1");var subQ18=sQuery(id+"F12.wireOp",EDGE,"E74.8");Q0=qUnion([makeQuery(id+"F12.imprint","IMPRINT",FACE,{"disambiguationData":[TD([[makeQuery(id+"F12.imprint","IMPRINT",EDGE,{"derivedFrom":subQ7}),1.0]])]}),makeQuery(id+"F12.imprint","IMPRINT",FACE,{"disambiguationData":[TD([[makeQuery(id+"F12.imprint","IMPRINT",EDGE,{"derivedFrom":subQ14}),1.0]])]}),makeQuery(id+"F12.imprint","IMPRINT",FACE,{"disambiguationData":[TD([[makeQuery(id+"F12.imprint","IMPRINT",EDGE,{"derivedFrom":subQ16}),1.0]])]}),makeQuery(id+"F12.imprint","IMPRINT",FACE,{"disambiguationData":[TD([[makeQuery(id+"F12.imprint","IMPRINT",EDGE,{"derivedFrom":subQ18}),-1.0]])]})]);}
            var Q1;
            Q1=makeQuery(id+"F5.boolean.opBoolean","SPLIT",FACE,{"disambiguationData":[TD([makeQuery(id+"F5.opExtrude","SWEPT_FACE",FACE,{"disambiguationData":[OSD([sQuery(id+"F4.wireOp",EDGE,"E41")])]})])],"derivedFrom":makeQuery(id+"F3.boolean.opBoolean","COPY",FACE,{"derivedFrom":makeQuery(id+"F3.opExtrude","CAP_FACE",FACE,{"disambiguationData":[OSD([sQuery(id+"F0.wireOp",EDGE,"E25.0"),sQuery(id+"F0.wireOp",EDGE,"E25.1"),sQuery(id+"F0.wireOp",EDGE,"E25.2"),sQuery(id+"F0.wireOp",EDGE,"E25.3"),sQuery(id+"F0.wireOp",EDGE,"E25.4"),sQuery(id+"F0.wireOp",EDGE,"E25.5"),sQuery(id+"F0.wireOp",EDGE,"E25.6"),sQuery(id+"F0.wireOp",EDGE,"E25.7")])],"isStart":false})})});
            extrude(context, id + "F13", {"entities" : qUnion([Q0]), "operationType" : NewBodyOperationType.REMOVE, "endBound" : BoundingType.UP_TO_SURFACE, "endBoundEntityFace" : qUnion([Q1]), "depth" : 25 * mm});
        }
        {
            var Q0;
            Q0=makeQuery(id+"F3.boolean.opBoolean","COPY",EDGE,{"derivedFrom":makeQuery(id+"F3.opExtrude","CAP_EDGE",EDGE,{"disambiguationData":[OSD([sQuery(id+"F0.wireOp",EDGE,"E25.6")])],"isStart":false})});
            var Q1;
            Q1=makeQuery(id+"F8.boolean.opBoolean","INTERSECT",EDGE,{"derivedFrom":[makeQuery(id+"F5.opExtrude","SWEPT_FACE",FACE,{"disambiguationData":[OSD([sQuery(id+"F4.wireOp",EDGE,"E30")])]}),makeQuery(id+"F8.opExtrude","CAP_FACE",FACE,{"disambiguationData":[OSD([sQuery(id+"F7.wireOp",EDGE,"E67")])],"isStart":false})]});
            var Q2;
            Q2=makeQuery(id+"F8.boolean.opBoolean","INTERSECT",EDGE,{"disambiguationData":[OD(1.0)],"derivedFrom":[makeQuery(id+"F5.opExtrude","SWEPT_FACE",FACE,{"disambiguationData":[OSD([sQuery(id+"F4.wireOp",EDGE,"E30")])]}),makeQuery(id+"F8.opExtrude","SWEPT_FACE",FACE,{"disambiguationData":[OSD([sQuery(id+"F7.wireOp",EDGE,"E67")])]})]});
            var Q3;
            {var subQ0=sQuery(id+"F4.wireOp",EDGE,"E30");Q3=makeQuery(id+"F8.boolean.opBoolean","SPLIT",EDGE,{"disambiguationData":[TD([makeQuery(id+"F5.opExtrude","SWEPT_FACE",FACE,{"disambiguationData":[OSD([sQuery(id+"F4.wireOp",EDGE,"E35.filletArc")])]})])],"derivedFrom":makeQuery(id+"F5.opExtrude","CAP_EDGE",EDGE,{"disambiguationData":[OSD([subQ0])],"isStart":false})});}
            var Q4;
            {var subQ0=sQuery(id+"F0.wireOp",EDGE,"E25.7");var subQ1=sQuery(id+"F0.wireOp",EDGE,"E25.1");var subQ2=sQuery(id+"F0.wireOp",EDGE,"E25.6");var subQ3=sQuery(id+"F0.wireOp",EDGE,"E25.5");var subQ4=sQuery(id+"F0.wireOp",EDGE,"E25.4");var subQ5=sQuery(id+"F0.wireOp",EDGE,"E25.0");var subQ6=sQuery(id+"F0.wireOp",EDGE,"E25.2");var subQ7=sQuery(id+"F0.wireOp",EDGE,"E25.3");Q4=makeQuery(id+"F8.boolean.opBoolean","INTERSECT",EDGE,{"derivedFrom":[makeQuery(id+"F5.boolean.opBoolean","SPLIT",FACE,{"disambiguationData":[TD([makeQuery(id+"F2.opExtrude","SWEPT_FACE",FACE,{"disambiguationData":[OSD([subQ5])]})])],"derivedFrom":makeQuery(id+"F3.boolean.opBoolean","COPY",FACE,{"derivedFrom":makeQuery(id+"F3.opExtrude","CAP_FACE",FACE,{"disambiguationData":[OSD([subQ5,subQ1,subQ6,subQ7,subQ4,subQ3,subQ2,subQ0])],"isStart":false})})}),makeQuery(id+"F8.opExtrude","SWEPT_FACE",FACE,{"disambiguationData":[OSD([sQuery(id+"F7.wireOp",EDGE,"E67")])]})]});}
            var Q5;
            Q5=makeQuery(id+"F8.boolean.opBoolean","INTERSECT",EDGE,{"disambiguationData":[OD(0.0)],"derivedFrom":[makeQuery(id+"F5.opExtrude","SWEPT_FACE",FACE,{"disambiguationData":[OSD([sQuery(id+"F4.wireOp",EDGE,"E30")])]}),makeQuery(id+"F8.opExtrude","SWEPT_FACE",FACE,{"disambiguationData":[OSD([sQuery(id+"F7.wireOp",EDGE,"E67")])]})]});
            fillet(context, id + "F14", {"entities" : qUnion([Q0, Q1, Q2, Q3, Q4, Q5]), "radius" : 3 * mm, "tangentPropagation" : true, "allowEdgeOverflow" : false});
        }
        {
            var Q0;
            Q0=makeQuery(id+"F1.opExtrude","CAP_EDGE",EDGE,{"disambiguationData":[OSD([sQuery(id+"F0.wireOp",EDGE,"E1.bottom")])],"isStart":false});
            fillet(context, id + "F15", {"entities" : qUnion([Q0]), "radius" : 2 * mm, "tangentPropagation" : true, "allowEdgeOverflow" : false});
        }
        {
            var Q0;
            {var subQ0=sQuery(id+"F0.wireOp",EDGE,"E22.filletArc");var subQ1=sQuery(id+"F0.wireOp",EDGE,"E7");var subQ2=sQuery(id+"F0.wireOp",EDGE,"E6");var subQ3=sQuery(id+"F0.wireOp",EDGE,"E5");var subQ4=sQuery(id+"F0.wireOp",EDGE,"E4");var subQ5=sQuery(id+"F0.wireOp",EDGE,"E1.bottom");var subQ6=sQuery(id+"F0.wireOp",EDGE,"E21.filletArc");var subQ7=sQuery(id+"F0.wireOp",EDGE,"E1.top");var subQ8=sQuery(id+"F0.wireOp",EDGE,"E1.left");var subQ9=sQuery(id+"F0.wireOp",EDGE,"E1.right");var subQ10=sQuery(id+"F0.wireOp",EDGE,"E23.filletArc");var subQ11=sQuery(id+"F0.wireOp",EDGE,"E24.filletArc");Q0=makeQuery(id+"F2.boolean.opBoolean","SPLIT",FACE,{"disambiguationData":[TD([makeQuery(id+"F1.opExtrude","SWEPT_FACE",FACE,{"disambiguationData":[OSD([subQ5])]})])],"derivedFrom":makeQuery(id+"F1.opExtrude","CAP_FACE",FACE,{"disambiguationData":[OSD([subQ5,subQ7,subQ8,subQ9,subQ4,subQ3,subQ2,subQ1,subQ6,subQ0,subQ10,subQ11])],"isStart":true})});}
            var sketch = newSketch(context, id + "F16", { "sketchPlane" : qUnion([Q0])});
            skLineSegment(sketch, "E79", {"start": v(0, 135) * mm, "end": v(0, 165) * mm, "construction": true});
            skArc(sketch, "E80", {"start": v(15, 165) * mm, "mid": v(0, 180) * mm, "end": v(-15, 165) * mm});
            skCircle(sketch, "E81", {"center": v(0, 165) * mm, "radius": 6 * mm});
            skLineSegment(sketch, "E82", {"start": v(-15, 165) * mm, "end": v(-15, 153) * mm});
            skLineSegment(sketch, "E83", {"start": v(15, 165) * mm, "end": v(15, 153) * mm});
            skLineSegment(sketch, "E84", {"start": v(-15, 153) * mm, "end": v(-33, 135) * mm});
            skLineSegment(sketch, "E85", {"start": v(15, 153) * mm, "end": v(33, 135) * mm});
            skLineSegment(sketch, "E86", {"start": v(-94.1, 0) * mm, "end": v(101.32, 0) * mm, "construction": true});
            skLineSegment(sketch, "E87.MirrorCS", {"start": v(-15, -153) * mm, "end": v(-33, -135) * mm});
            skArc(sketch, "E88.MirrorCS", {"start": v(15, -165) * mm, "mid": v(0, -180) * mm, "end": v(-15, -165) * mm});
            skLineSegment(sketch, "E89.MirrorCS", {"start": v(15, -165) * mm, "end": v(15, -153) * mm});
            skLineSegment(sketch, "E90.MirrorCS", {"start": v(15, -153) * mm, "end": v(33, -135) * mm});
            skLineSegment(sketch, "E91.MirrorCS", {"start": v(-15, -165) * mm, "end": v(-15, -153) * mm});
            skCircle(sketch, "E92.MirrorC", {"center": v(0, -165) * mm, "radius": 6 * mm});
            skLineSegment(sketch, "E93", {"start": v(-33, 135) * mm, "end": v(33, 135) * mm});
            skLineSegment(sketch, "E94.MirrorCS", {"start": v(-33, -135) * mm, "end": v(33, -135) * mm});
            skSolve(sketch);
        }
        {
            var Q0;
            Q0=makeQuery(id+"F16.imprint","IMPRINT",FACE,{"disambiguationData":[TD([[makeQuery(id+"F16.imprint","IMPRINT",EDGE,{"derivedFrom":sQuery(id+"F16.wireOp",EDGE,"E80")}),1.0]])]});
            var Q1;
            Q1=makeQuery(id+"F16.imprint","IMPRINT",FACE,{"disambiguationData":[TD([[makeQuery(id+"F16.imprint","IMPRINT",EDGE,{"derivedFrom":sQuery(id+"F16.wireOp",EDGE,"E87.MirrorCS")}),-1.0]])]});
            var Q2;
            {var subQ4=sQuery(id+"F16.wireOp",EDGE,"E93");Q2=makeQuery(id+"F16.imprint","IMPRINT",FACE,{"disambiguationData":[TD([[makeQuery(id+"F16.imprint","IMPRINT",EDGE,{"derivedFrom":subQ4}),-1.0]])]});}
            var Q3;
            Q3=makeQuery(id+"F2.opExtrude","CAP_FACE",FACE,{"disambiguationData":[OSD([sQuery(id+"F0.wireOp",EDGE,"E12"),sQuery(id+"F0.wireOp",EDGE,"E13"),sQuery(id+"F0.wireOp",EDGE,"E14"),sQuery(id+"F0.wireOp",EDGE,"E15"),sQuery(id+"F0.wireOp",EDGE,"E17.filletArc"),sQuery(id+"F0.wireOp",EDGE,"E18.filletArc"),sQuery(id+"F0.wireOp",EDGE,"E19.filletArc"),sQuery(id+"F0.wireOp",EDGE,"E20.filletArc"),sQuery(id+"F0.wireOp",EDGE,"E25.0"),sQuery(id+"F0.wireOp",EDGE,"E25.1"),sQuery(id+"F0.wireOp",EDGE,"E25.2"),sQuery(id+"F0.wireOp",EDGE,"E25.3"),sQuery(id+"F0.wireOp",EDGE,"E25.4"),sQuery(id+"F0.wireOp",EDGE,"E25.5"),sQuery(id+"F0.wireOp",EDGE,"E25.6"),sQuery(id+"F0.wireOp",EDGE,"E25.7")])],"isStart":false});
            extrude(context, id + "F17", {"entities" : qUnion([Q0, Q1, Q2]), "endBound" : BoundingType.UP_TO_SURFACE, "endBoundEntityFace" : qUnion([Q3]), "depth" : 25 * mm});
        }
    });
